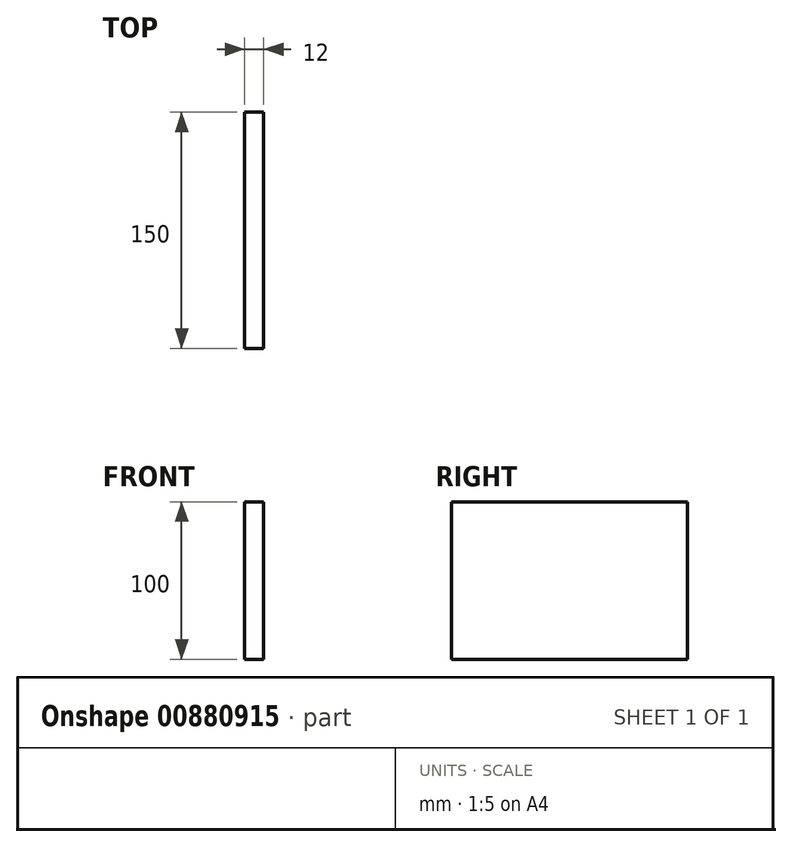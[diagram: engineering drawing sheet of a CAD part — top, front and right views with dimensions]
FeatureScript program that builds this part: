
annotation { "Feature Type Name" : "Feature", "Feature Type Description" : "" }
export const myFeature = defineFeature(function(context is Context, id is Id, definition is map)
    precondition{}
    {
        {
            var Q0;
            Q0=qCreatedBy(makeId("Top.planeOp"),FACE);
            var sketch = newSketch(context, id + "F0", { "sketchPlane" : qUnion([Q0])});
            skLineSegment(sketch, "E0.right", {"start": v(-6, 75) * mm, "end": v(-6, -75) * mm});
            skPoint(sketch, "E1.orphan", {"position": v(6, -75) * mm});
            skLineSegment(sketch, "E2", {"start": v(-6, -75) * mm, "end": v(6, -75) * mm});
            skLineSegment(sketch, "E3", {"start": v(-6, 75) * mm, "end": v(6, 75) * mm});
            skLineSegment(sketch, "E4", {"start": v(6, -75) * mm, "end": v(6, 75) * mm});
            skSolve(sketch);
        }
        {
            var Q0;
            Q0 = qSketchRegion(id + "F0", true);
            extrude(context, id + "F1", {"entities" : qUnion([Q0]), "oppositeDirection" : true, "depth" : 100 * mm, "offsetDistance" : 25 * mm});
        }
    });
